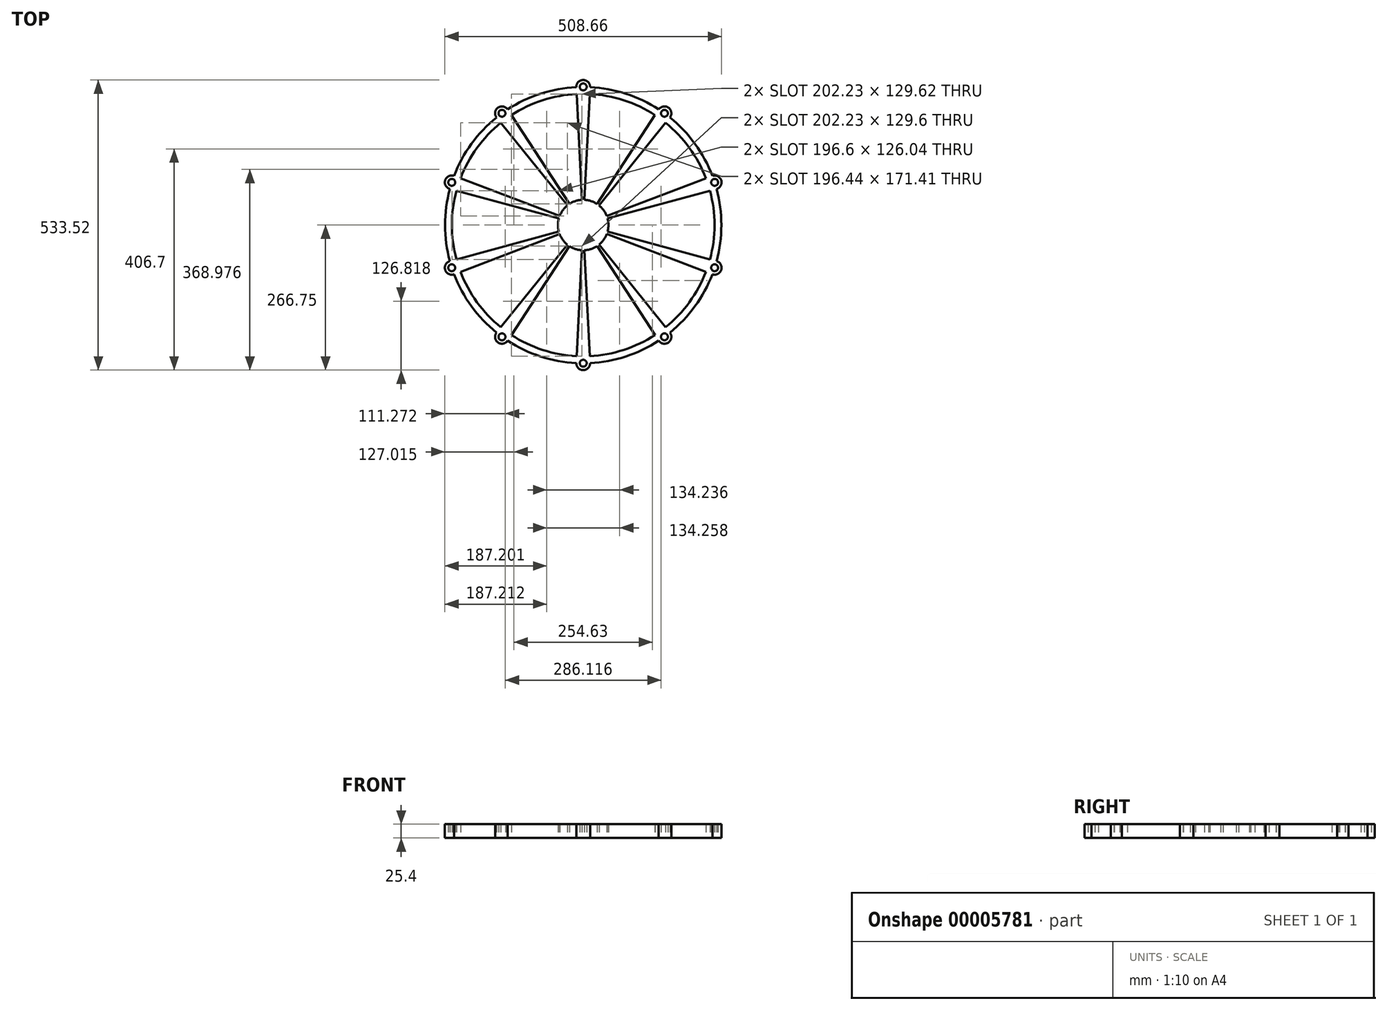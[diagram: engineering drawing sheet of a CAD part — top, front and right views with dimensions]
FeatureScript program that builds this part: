
annotation { "Feature Type Name" : "Feature", "Feature Type Description" : "" }
export const myFeature = defineFeature(function(context is Context, id is Id, definition is map)
    precondition{}
    {
        {
            var Q0;
            Q0=qCreatedBy(makeId("Top.planeOp"),FACE);
            var sketch = newSketch(context, id + "F0", { "sketchPlane" : qUnion([Q0])});
            skArc(sketch, "E0", {"start": v(138.83, 212.7) * mm, "mid": v(78.48, 241.57) * mm, "end": v(12.68, 253.68) * mm});
            skArc(sketch, "E1", {"start": v(12.68, 253.68) * mm, "mid": v(-0.01, 266.76) * mm, "end": v(-12.7, 253.68) * mm});
            skCircle(sketch, "E2", {"center": v(-0.01, 254.06) * mm, "radius": 6.35 * mm});
            skArc(sketch, "E3", {"start": v(12.68, 253.68) * mm, "mid": v(-0.01, 254) * mm, "end": v(-12.7, 253.68) * mm, "construction": true});
            skArc(sketch, "E4.1.0", {"start": v(-12.7, 253.68) * mm, "mid": v(-78.5, 241.56) * mm, "end": v(-138.85, 212.69) * mm});
            skArc(sketch, "E4.1.1", {"start": v(-138.85, 212.69) * mm, "mid": v(-156.8, 215.8) * mm, "end": v(-159.39, 197.76) * mm});
            skCircle(sketch, "E4.1.2", {"center": v(-149.34, 205.53) * mm, "radius": 6.35 * mm});
            skArc(sketch, "E4.1.3", {"start": v(-138.85, 212.69) * mm, "mid": v(-149.3, 205.48) * mm, "end": v(-159.39, 197.76) * mm, "construction": true});
            skArc(sketch, "E4.2.0", {"start": v(-159.39, 197.76) * mm, "mid": v(-205.5, 149.29) * mm, "end": v(-237.35, 90.45) * mm});
            skArc(sketch, "E4.2.1", {"start": v(-237.35, 90.45) * mm, "mid": v(-253.7, 82.42) * mm, "end": v(-245.2, 66.3) * mm});
            skCircle(sketch, "E4.2.2", {"center": v(-241.63, 78.5) * mm, "radius": 6.35 * mm});
            skArc(sketch, "E4.2.3", {"start": v(-237.35, 90.45) * mm, "mid": v(-241.57, 78.48) * mm, "end": v(-245.2, 66.3) * mm, "construction": true});
            skArc(sketch, "E4.3.0", {"start": v(-245.2, 66.3) * mm, "mid": v(-254, -0.01) * mm, "end": v(-245.19, -66.33) * mm});
            skArc(sketch, "E4.3.1", {"start": v(-245.19, -66.33) * mm, "mid": v(-253.7, -82.44) * mm, "end": v(-237.34, -90.48) * mm});
            skCircle(sketch, "E4.3.2", {"center": v(-241.62, -78.52) * mm, "radius": 6.35 * mm});
            skArc(sketch, "E4.3.3", {"start": v(-245.19, -66.33) * mm, "mid": v(-241.56, -78.5) * mm, "end": v(-237.34, -90.48) * mm, "construction": true});
            skArc(sketch, "E4.4.0", {"start": v(-237.34, -90.48) * mm, "mid": v(-205.48, -149.3) * mm, "end": v(-159.37, -197.78) * mm});
            skArc(sketch, "E4.4.1", {"start": v(-159.37, -197.78) * mm, "mid": v(-156.79, -215.82) * mm, "end": v(-138.83, -212.7) * mm});
            skCircle(sketch, "E4.4.2", {"center": v(-149.32, -205.54) * mm, "radius": 6.35 * mm});
            skArc(sketch, "E4.4.3", {"start": v(-159.37, -197.78) * mm, "mid": v(-149.29, -205.5) * mm, "end": v(-138.83, -212.7) * mm, "construction": true});
            skArc(sketch, "E4.5.0", {"start": v(-138.83, -212.7) * mm, "mid": v(-78.48, -241.57) * mm, "end": v(-12.68, -253.68) * mm});
            skArc(sketch, "E4.5.1", {"start": v(-12.68, -253.68) * mm, "mid": v(0.01, -266.76) * mm, "end": v(12.7, -253.68) * mm});
            skCircle(sketch, "E4.5.2", {"center": v(0.01, -254.06) * mm, "radius": 6.35 * mm});
            skArc(sketch, "E4.5.3", {"start": v(-12.68, -253.68) * mm, "mid": v(0.01, -254) * mm, "end": v(12.7, -253.68) * mm, "construction": true});
            skArc(sketch, "E4.6.0", {"start": v(12.7, -253.68) * mm, "mid": v(78.5, -241.56) * mm, "end": v(138.85, -212.69) * mm});
            skArc(sketch, "E4.6.1", {"start": v(138.85, -212.69) * mm, "mid": v(156.8, -215.8) * mm, "end": v(159.39, -197.76) * mm});
            skCircle(sketch, "E4.6.2", {"center": v(149.34, -205.53) * mm, "radius": 6.35 * mm});
            skArc(sketch, "E4.6.3", {"start": v(138.85, -212.69) * mm, "mid": v(149.3, -205.48) * mm, "end": v(159.39, -197.76) * mm, "construction": true});
            skArc(sketch, "E4.7.0", {"start": v(159.39, -197.76) * mm, "mid": v(205.5, -149.29) * mm, "end": v(237.35, -90.45) * mm});
            skArc(sketch, "E4.7.1", {"start": v(237.35, -90.45) * mm, "mid": v(253.7, -82.42) * mm, "end": v(245.2, -66.3) * mm});
            skCircle(sketch, "E4.7.2", {"center": v(241.63, -78.5) * mm, "radius": 6.35 * mm});
            skArc(sketch, "E4.7.3", {"start": v(237.35, -90.45) * mm, "mid": v(241.57, -78.48) * mm, "end": v(245.2, -66.3) * mm, "construction": true});
            skArc(sketch, "E4.8.0", {"start": v(245.2, -66.3) * mm, "mid": v(254, 0.01) * mm, "end": v(245.19, 66.33) * mm});
            skArc(sketch, "E4.8.1", {"start": v(245.19, 66.33) * mm, "mid": v(253.7, 82.44) * mm, "end": v(237.34, 90.48) * mm});
            skCircle(sketch, "E4.8.2", {"center": v(241.62, 78.52) * mm, "radius": 6.35 * mm});
            skArc(sketch, "E4.8.3", {"start": v(245.19, 66.33) * mm, "mid": v(241.56, 78.5) * mm, "end": v(237.34, 90.48) * mm, "construction": true});
            skArc(sketch, "E4.9.0", {"start": v(237.34, 90.48) * mm, "mid": v(205.48, 149.3) * mm, "end": v(159.37, 197.78) * mm});
            skArc(sketch, "E4.9.1", {"start": v(159.37, 197.78) * mm, "mid": v(156.79, 215.82) * mm, "end": v(138.83, 212.7) * mm});
            skCircle(sketch, "E4.9.2", {"center": v(149.32, 205.54) * mm, "radius": 6.35 * mm});
            skArc(sketch, "E4.9.3", {"start": v(159.37, 197.78) * mm, "mid": v(149.29, 205.5) * mm, "end": v(138.83, 212.7) * mm, "construction": true});
            skArc(sketch, "E5", {"start": v(-12.07, 241.05) * mm, "mid": v(-74.6, 229.54) * mm, "end": v(-131.94, 202.1) * mm});
            skArc(sketch, "E6", {"start": v(-2.32, 46.31) * mm, "mid": v(-14.33, 44.1) * mm, "end": v(-25.35, 38.83) * mm});
            skLineSegment(sketch, "E7", {"start": v(-12.07, 241.05) * mm, "end": v(-2.32, 46.31) * mm});
            skLineSegment(sketch, "E8", {"start": v(12.05, 241.05) * mm, "end": v(2.32, 46.31) * mm});
            skLineSegment(sketch, "E9.1.0", {"start": v(-151.46, 187.92) * mm, "end": v(-29.1, 36.1) * mm});
            skLineSegment(sketch, "E9.1.1", {"start": v(-131.94, 202.1) * mm, "end": v(-25.35, 38.83) * mm});
            skLineSegment(sketch, "E9.2.0", {"start": v(-232.99, 63) * mm, "end": v(-44.76, 12.1) * mm});
            skLineSegment(sketch, "E9.2.1", {"start": v(-225.53, 85.95) * mm, "end": v(-43.33, 16.51) * mm});
            skLineSegment(sketch, "E9.3.0", {"start": v(-225.53, -85.97) * mm, "end": v(-43.33, -16.52) * mm});
            skLineSegment(sketch, "E9.3.1", {"start": v(-232.98, -63.03) * mm, "end": v(-44.76, -12.1) * mm});
            skLineSegment(sketch, "E9.4.0", {"start": v(-131.92, -202.11) * mm, "end": v(-25.34, -38.83) * mm});
            skLineSegment(sketch, "E9.4.1", {"start": v(-151.44, -187.93) * mm, "end": v(-29.1, -36.1) * mm});
            skLineSegment(sketch, "E9.5.0", {"start": v(12.07, -241.05) * mm, "end": v(2.32, -46.31) * mm});
            skLineSegment(sketch, "E9.5.1", {"start": v(-12.05, -241.05) * mm, "end": v(-2.32, -46.31) * mm});
            skLineSegment(sketch, "E9.6.0", {"start": v(151.46, -187.92) * mm, "end": v(29.1, -36.1) * mm});
            skLineSegment(sketch, "E9.6.1", {"start": v(131.94, -202.1) * mm, "end": v(25.35, -38.83) * mm});
            skLineSegment(sketch, "E9.7.0", {"start": v(232.99, -63) * mm, "end": v(44.76, -12.1) * mm});
            skLineSegment(sketch, "E9.7.1", {"start": v(225.53, -85.95) * mm, "end": v(43.33, -16.51) * mm});
            skLineSegment(sketch, "E9.8.0", {"start": v(225.53, 85.97) * mm, "end": v(43.33, 16.52) * mm});
            skLineSegment(sketch, "E9.8.1", {"start": v(232.98, 63.03) * mm, "end": v(44.76, 12.1) * mm});
            skLineSegment(sketch, "E9.9.0", {"start": v(131.92, 202.11) * mm, "end": v(25.34, 38.83) * mm});
            skLineSegment(sketch, "E9.9.1", {"start": v(151.44, 187.93) * mm, "end": v(29.1, 36.1) * mm});
            skArc(sketch, "E10.trimOffspring", {"start": v(131.92, 202.11) * mm, "mid": v(74.57, 229.55) * mm, "end": v(12.05, 241.05) * mm});
            skArc(sketch, "E11.trimOffspring", {"start": v(225.53, 85.97) * mm, "mid": v(195.25, 141.87) * mm, "end": v(151.44, 187.93) * mm});
            skArc(sketch, "E12.trimOffspring", {"start": v(232.99, -63) * mm, "mid": v(241.36, 0.01) * mm, "end": v(232.98, 63.03) * mm});
            skArc(sketch, "E13.trimOffspring", {"start": v(151.46, -187.92) * mm, "mid": v(195.27, -141.86) * mm, "end": v(225.53, -85.95) * mm});
            skArc(sketch, "E14.trimOffspring", {"start": v(12.07, -241.05) * mm, "mid": v(74.6, -229.54) * mm, "end": v(131.94, -202.1) * mm});
            skArc(sketch, "E15.trimOffspring", {"start": v(-131.92, -202.11) * mm, "mid": v(-74.57, -229.55) * mm, "end": v(-12.05, -241.05) * mm});
            skArc(sketch, "E16.trimOffspring", {"start": v(-225.53, -85.97) * mm, "mid": v(-195.25, -141.87) * mm, "end": v(-151.44, -187.93) * mm});
            skArc(sketch, "E17.trimOffspring", {"start": v(-232.99, 63) * mm, "mid": v(-241.36, -0.01) * mm, "end": v(-232.98, -63.03) * mm});
            skArc(sketch, "E18.trimOffspring", {"start": v(-151.46, 187.92) * mm, "mid": v(-195.27, 141.86) * mm, "end": v(-225.53, 85.95) * mm});
            skArc(sketch, "E19.trimOffspring", {"start": v(-29.1, 36.1) * mm, "mid": v(-37.51, 27.25) * mm, "end": v(-43.33, 16.51) * mm});
            skArc(sketch, "E20.trimOffspring", {"start": v(-44.76, 12.1) * mm, "mid": v(-46.37, 0) * mm, "end": v(-44.76, -12.1) * mm});
            skArc(sketch, "E21.trimOffspring", {"start": v(-43.33, -16.52) * mm, "mid": v(-37.51, -27.26) * mm, "end": v(-29.1, -36.1) * mm});
            skArc(sketch, "E22.trimOffspring", {"start": v(-25.34, -38.83) * mm, "mid": v(-14.33, -44.1) * mm, "end": v(-2.32, -46.31) * mm});
            skArc(sketch, "E23.trimOffspring", {"start": v(2.32, -46.31) * mm, "mid": v(14.33, -44.1) * mm, "end": v(25.35, -38.83) * mm});
            skArc(sketch, "E24.trimOffspring", {"start": v(29.1, -36.1) * mm, "mid": v(37.51, -27.25) * mm, "end": v(43.33, -16.51) * mm});
            skArc(sketch, "E25.trimOffspring", {"start": v(44.76, -12.1) * mm, "mid": v(46.37, 0) * mm, "end": v(44.76, 12.1) * mm});
            skArc(sketch, "E26.trimOffspring", {"start": v(43.33, 16.52) * mm, "mid": v(37.51, 27.26) * mm, "end": v(29.1, 36.1) * mm});
            skArc(sketch, "E27.trimOffspring", {"start": v(25.34, 38.83) * mm, "mid": v(14.33, 44.1) * mm, "end": v(2.32, 46.31) * mm});
            skSolve(sketch);
        }
        {
            var Q0;
            Q0=makeQuery(id+"F0.imprint","IMPRINT",FACE,{"disambiguationData":[TD([[makeQuery(id+"F0.imprint","IMPRINT",EDGE,{"derivedFrom":sQuery(id+"F0.wireOp",EDGE,"E0")}),1.0]])]});
            extrude(context, id + "F1", {"entities" : qUnion([Q0]), "depth" : 25.4 * mm});
        }
    });
